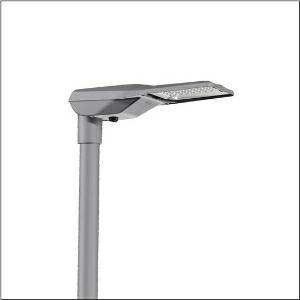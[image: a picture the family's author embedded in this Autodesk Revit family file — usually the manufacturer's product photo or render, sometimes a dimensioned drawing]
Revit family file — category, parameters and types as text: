
# Revit family: streetlight_sl_21_iq_mini___st1_0a_5xe2d31u08gb_76f1
name_source: partatom
category: Lighting Fixtures
units: mm (PartAtom-declared; Revit-internal decimal feet)

## family parameters
Cut with Voids When Loaded = No
Host = Face
Light Source = No
Part Type = Normal
Room Calculation Point = No
Round Connector Dimension = Use Diameter
Shared = No

## types (1)
- --- (1 x LED, 5990 lm, 39.8 W, 3000K)
    Apparent Load = 40 VA
    CIE Flux Codes = 37 72 97 100 100
    Color Rendering = 70
    Color Temperature = 3000K
    Default Elevation = 1800 mm
    Description = Streetlight SL 21 iQ mini, mast luminaire, primary light control with lens, of PMMA, primary optical cover: cover, of toughened safety glass, transparent, light distribution: ST1.0a, light emission: direct distribution, primary light characteristic: asymmetric, installation type: post-top, side-entry, LED, High Power LED, rated luminous flux: 5.990lm, luminous efficacy: 151lm/W, light colour: 730, colour temperature: 3000K, control gear: iQ-Street Remote, D4i with power reduction, control: pre-setting: logarithmic dimming characteristic, Street-Remote, Auto-Match, Temp-Guard, Lumen-Switch, Night-Set, Smart-Wire, Light-Fading, Desk-Remote (wireless, voltage-free reading and setting of iQ features in the workshop via application-optimized NFC function/RFID function), optimised constant luminous flux control (CLO 2.0), mains connection: 220..240V, AC, 50/60Hz, start of lifetime: 40W, end of service life: 41W, reduction: 18W, luminaire housing, of diecast aluminium, powder-coated, SITECO metallic grey (DB 702S), corrosivity category C5 high according to DIN EN ISO 12944, please order mast flange separately, inclination adjustable: 0°, 5°, 10°, 15°, sealing non-destructively replaceable, multi-level sealing system, length: 628mm, width: 235mm, height: 110mm, mast flange for spigot size: 42mm (side-entry): 5XC10008XM4, 60/48mm (side-entry/post-top): 5XC10108XM2, 76/60mm (side-entry/post-top): 5XC10108XM1, mounting height: 4..8m, Smart Interface below, protection rating (complete): IP66, insulation class (complete): insulation class II (safety insulation), certification: CE, ENEC, ENEC+, VDE, impact resistance: IK10, permissible operating ambient temperature for outdoor applications: -40..+50°C, standard-compliant lighting for roads and squares, packaging unit: 1 piece

Light Distribution: ST1.0a
    Height = 110 mm
    Lamp = 1 x LED
    Lamp Light Flux = 5990 lm
    Lamp Power = 39.8 W
    Lamp count = 1
    Length = 625 mm
    Luminous efficacy = 151 lm/W
    Manufacturer = Siteco
    ModVariant = No
    Model = 5XE2D31U08GB
    Number of Poles = 1
    OnlyDefault = Yes
    Power Factor = 1
    Product Name = Streetlight SL 21 iQ mini | ST1.0a
    Product group = mast luminaire | pylon top
    ProductGroupID = 6100
    Protection Class = Protection class II
    Protection Degree = IP 66
    RLX_Detail_Level = 1
    RLX_Emergency_Light_Flux = 0 lm
    RLX_Emergency_Type = 0
    RLX_Emergency_Type_DB = No
    RlxData = <blob elided: 92861 chars, md5=db687d29>
    Socket = socket
    Standby Power = 0 W
    System Light Flux = 5990 lm
    System Power = 40 W
    Type Comments = factory setting: luminous flux: 100 % | dim-lin: 254 | 800 mA
    Type Image = l_1003516.jpg
    URL = http://relux.com
    VarID = @adj_115349
    Voltage = 0 V
    Weight = 0.00 kg
    Width = 234 mm

## geometry (parser evidence)
native form markers: Blend x4, Sweep x10
no freeform markers — native parametric forms only
